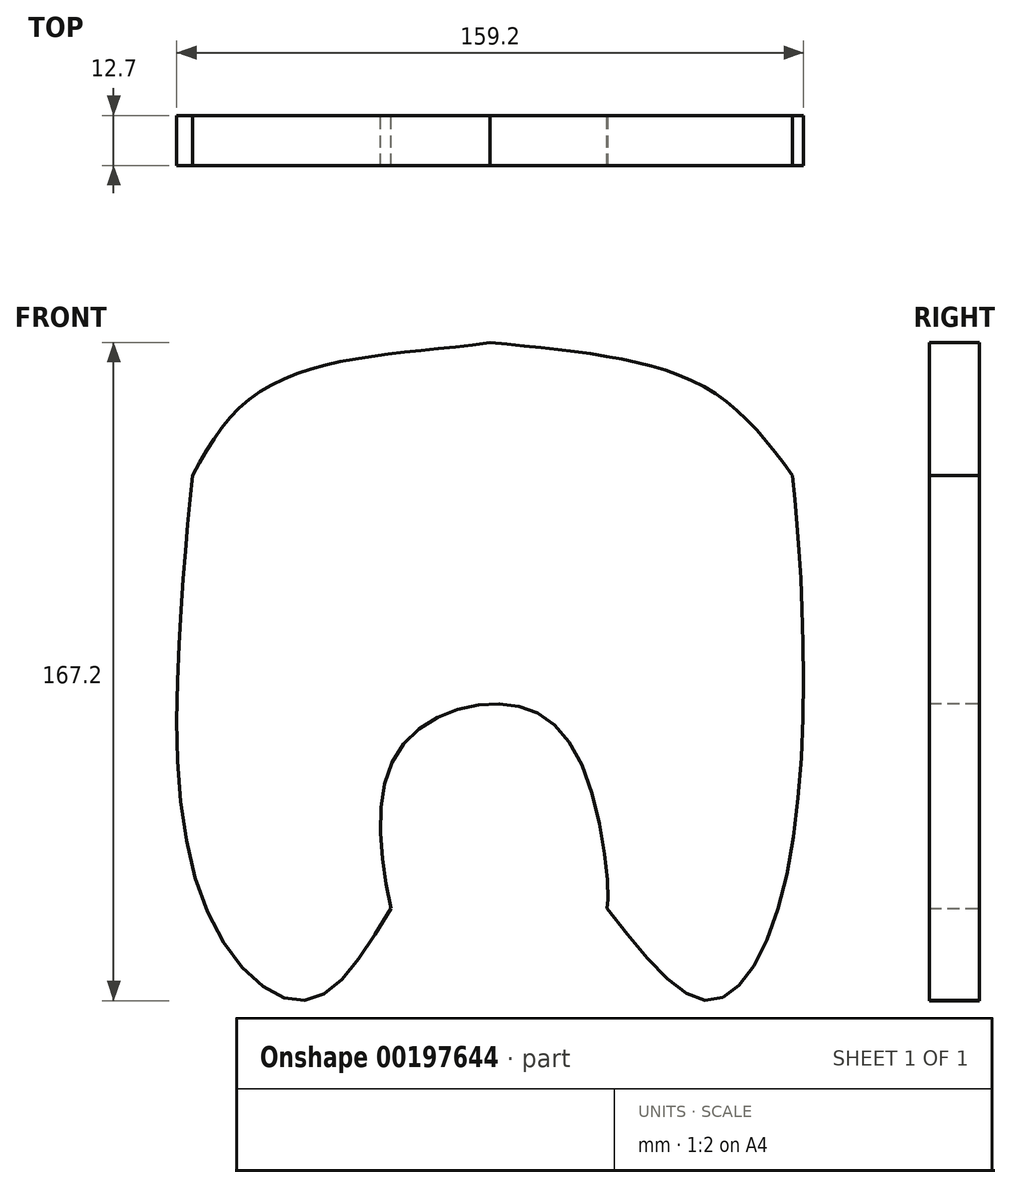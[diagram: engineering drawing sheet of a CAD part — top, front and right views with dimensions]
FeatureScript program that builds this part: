
annotation { "Feature Type Name" : "Feature", "Feature Type Description" : "" }
export const myFeature = defineFeature(function(context is Context, id is Id, definition is map)
    precondition{}
    {
        {
            var Q0;
            Q0=qCreatedBy(makeId("Front.planeOp"),FACE);
            var sketch = newSketch(context, id + "F0", { "sketchPlane" : qUnion([Q0])});
            skFitSpline(sketch, "E0", {"points": [v(-25.16, -72.44) * mm, v(-24.28, -34.23) * mm, v(0, -20.5) * mm, v(22.53, -34.23) * mm, v(29.75, -72.44) * mm, v(29.32, -72.44) * mm], "startDerivative": vector(-29.8, 139.24) * mm, "endDerivative": vector(-16.06, 8.35) * mm});
            skFitSpline(sketch, "E1", {"points": [v(0, 71.27) * mm, v(-36.8, 66.65) * mm, v(-61.18, 56.8) * mm, v(-75.5, 37.56) * mm], "startDerivative": vector(-100.78, -14.07) * mm, "endDerivative": vector(-39.52, -74.97) * mm});
            skFitSpline(sketch, "E2", {"points": [v(0, 71.27) * mm, v(35.5, 66.65) * mm, v(59.46, 56.8) * mm, v(76.9, 37.56) * mm], "startDerivative": vector(100.14, -9.23) * mm, "endDerivative": vector(51.05, -67.83) * mm});
            skFitSpline(sketch, "E3", {"points": [v(-75.5, 37.56) * mm, v(-78.68, 0) * mm, v(-72.2, -72.44) * mm, v(-46.8, -95.86) * mm, v(-25.16, -72.44) * mm], "startDerivative": vector(-14.4, -141.31) * mm, "endDerivative": vector(92.2, 156.06) * mm});
            skFitSpline(sketch, "E4", {"points": [v(76.9, 37.56) * mm, v(79.48, 0) * mm, v(73.3, -72.44) * mm, v(55.8, -95.86) * mm, v(29.75, -72.44) * mm], "startDerivative": vector(13.43, -140.63) * mm, "endDerivative": vector(-119.4, 154.73) * mm});
            skSolve(sketch);
        }
        {
            var Q0;
            Q0=makeQuery(id+"F0.imprint","IMPRINT",FACE,{"disambiguationData":[TD([[makeQuery(id+"F0.imprint","IMPRINT",EDGE,{"derivedFrom":sQuery(id+"F0.wireOp",EDGE,"E1")}),1.0]])]});
            extrude(context, id + "F1", {"entities" : qUnion([Q0]), "endBound" : BoundingType.SYMMETRIC, "depth" : 12.7 * mm});
        }
    });
